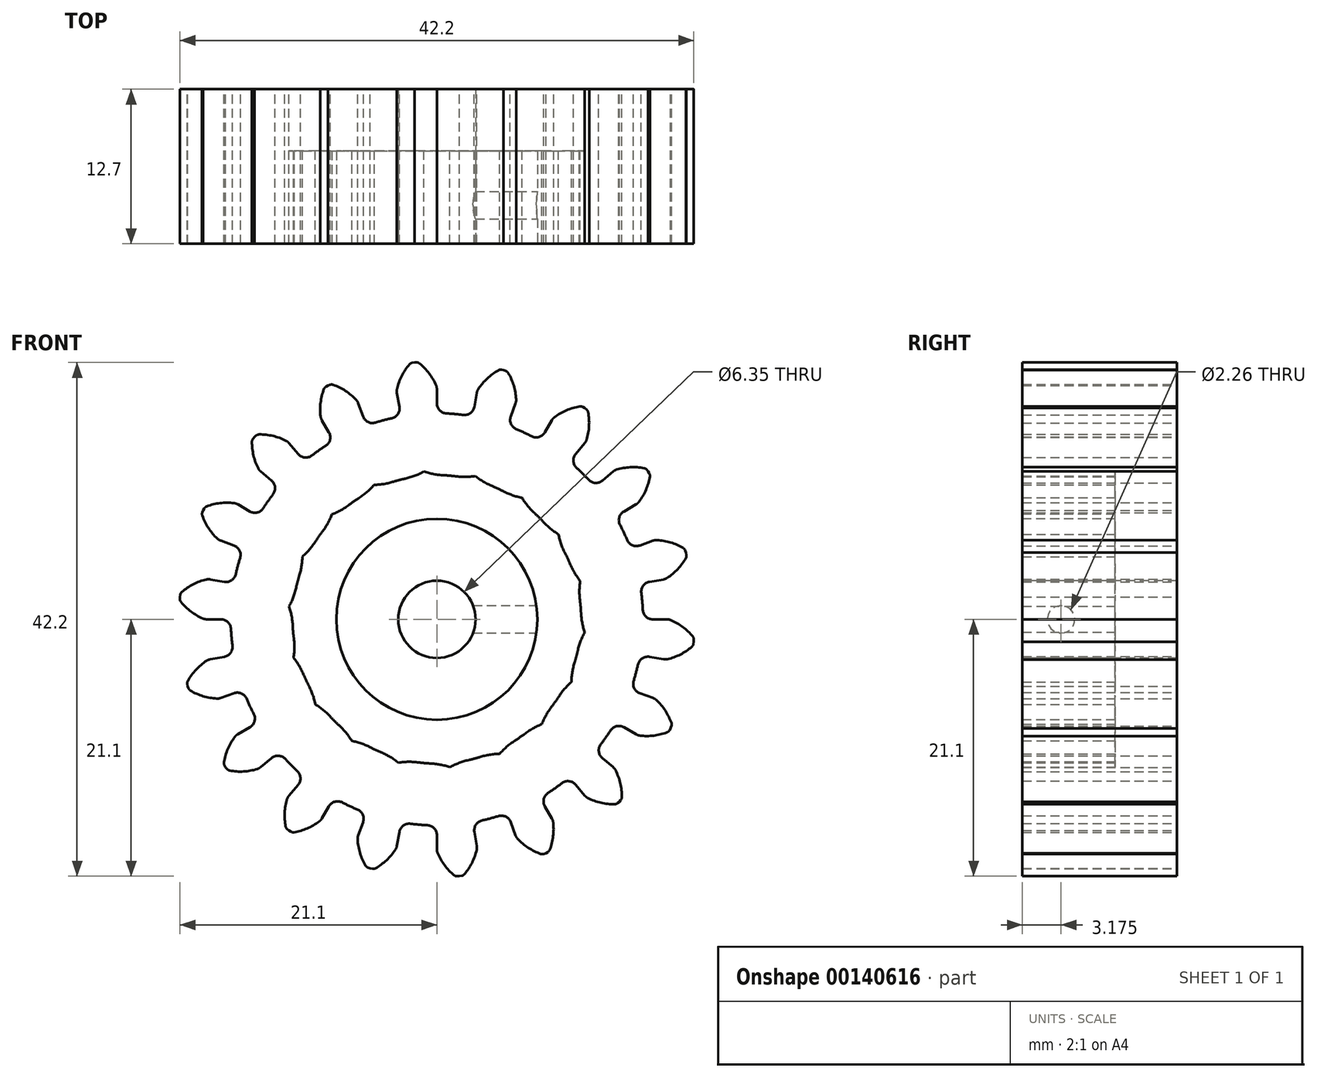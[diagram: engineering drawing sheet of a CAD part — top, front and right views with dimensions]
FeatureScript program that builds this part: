
annotation { "Feature Type Name" : "Feature", "Feature Type Description" : "" }
export const myFeature = defineFeature(function(context is Context, id is Id, definition is map)
    precondition{}
    {
        {
            var Q0;
            Q0=qCreatedBy(makeId("Front.planeOp"),FACE);
            var sketch = newSketch(context, id + "F0", { "sketchPlane" : qUnion([Q0])});
            skArc(sketch, "E0", {"start": v(-3.71, 16.52) * mm, "mid": v(-4.38, 16.35) * mm, "end": v(-5.04, 16.16) * mm});
            skArc(sketch, "E1.trimOffspring", {"start": v(-0.07, 19.21) * mm, "mid": v(-0.63, 20.2) * mm, "end": v(-1.42, 21.02) * mm});
            skLineSegment(sketch, "E2", {"start": v(0, 18.89) * mm, "end": v(0, 17.74) * mm});
            skLineSegment(sketch, "E3", {"start": v(-1.66, 21.1) * mm, "end": v(-1.85, 21.1) * mm});
            skLineSegment(sketch, "E4.MirrorCS", {"start": v(-2.03, 21.07) * mm, "end": v(-1.85, 21.1) * mm});
            skArc(sketch, "E5.MirrorCS", {"start": v(-3.27, 18.93) * mm, "mid": v(-2.88, 20) * mm, "end": v(-2.25, 20.94) * mm});
            skLineSegment(sketch, "E6.MirrorCS", {"start": v(-3.28, 18.6) * mm, "end": v(-3.08, 17.47) * mm});
            skPoint(sketch, "E7.visualSharp", {"position": v(0, 19.05) * mm});
            skArc(sketch, "E7.filletArc", {"start": v(0, 18.89) * mm, "mid": v(-0.02, 19.05) * mm, "end": v(-0.07, 19.21) * mm});
            skPoint(sketch, "E8.visualSharp", {"position": v(-3.3, 18.76) * mm});
            skArc(sketch, "E8.filletArc", {"start": v(-3.27, 18.93) * mm, "mid": v(-3.3, 18.77) * mm, "end": v(-3.28, 18.6) * mm});
            skPoint(sketch, "E9.visualSharp", {"position": v(-2.94, 16.67) * mm});
            skArc(sketch, "E9.filletArc", {"start": v(-3.71, 16.52) * mm, "mid": v(-3.2, 16.86) * mm, "end": v(-3.08, 17.47) * mm});
            skPoint(sketch, "E10.visualSharp", {"position": v(0, 16.93) * mm});
            skArc(sketch, "E10.filletArc", {"start": v(0, 17.74) * mm, "mid": v(0.23, 17.17) * mm, "end": v(0.79, 16.91) * mm});
            skPoint(sketch, "E11.visualSharp", {"position": v(-2.16, 21.05) * mm});
            skArc(sketch, "E11.filletArc", {"start": v(-2.03, 21.07) * mm, "mid": v(-2.15, 21.03) * mm, "end": v(-2.25, 20.94) * mm});
            skPoint(sketch, "E12.visualSharp", {"position": v(-1.53, 21.1) * mm});
            skArc(sketch, "E12.filletArc", {"start": v(-1.42, 21.02) * mm, "mid": v(-1.53, 21.08) * mm, "end": v(-1.66, 21.1) * mm});
            skArc(sketch, "E13.1.0", {"start": v(-9.14, 14.25) * mm, "mid": v(-8.78, 14.75) * mm, "end": v(-8.87, 15.36) * mm});
            skLineSegment(sketch, "E13.1.1", {"start": v(-9.44, 16.36) * mm, "end": v(-8.87, 15.36) * mm});
            skArc(sketch, "E13.1.2", {"start": v(-9.55, 16.67) * mm, "mid": v(-9.51, 16.51) * mm, "end": v(-9.44, 16.36) * mm});
            skArc(sketch, "E13.1.3", {"start": v(-9.55, 16.67) * mm, "mid": v(-9.55, 17.8) * mm, "end": v(-9.28, 18.9) * mm});
            skArc(sketch, "E13.1.4", {"start": v(-9.11, 19.1) * mm, "mid": v(-9.22, 19.02) * mm, "end": v(-9.28, 18.9) * mm});
            skLineSegment(sketch, "E13.1.5", {"start": v(-9.11, 19.1) * mm, "end": v(-8.95, 19.2) * mm});
            skLineSegment(sketch, "E13.1.6", {"start": v(-8.78, 19.26) * mm, "end": v(-8.95, 19.2) * mm});
            skArc(sketch, "E13.1.7", {"start": v(-8.52, 19.26) * mm, "mid": v(-8.65, 19.29) * mm, "end": v(-8.78, 19.26) * mm});
            skArc(sketch, "E13.1.8", {"start": v(-6.63, 18.03) * mm, "mid": v(-7.5, 18.76) * mm, "end": v(-8.52, 19.26) * mm});
            skArc(sketch, "E13.1.9", {"start": v(-6.46, 17.75) * mm, "mid": v(-6.53, 17.9) * mm, "end": v(-6.63, 18.03) * mm});
            skLineSegment(sketch, "E13.1.10", {"start": v(-6.46, 17.75) * mm, "end": v(-6.07, 16.67) * mm});
            skArc(sketch, "E13.1.11", {"start": v(-6.07, 16.67) * mm, "mid": v(-5.66, 16.2) * mm, "end": v(-5.04, 16.16) * mm});
            skArc(sketch, "E13.2.0", {"start": v(-13.46, 10.27) * mm, "mid": v(-13.3, 10.86) * mm, "end": v(-13.59, 11.4) * mm});
            skLineSegment(sketch, "E13.2.1", {"start": v(-14.47, 12.14) * mm, "end": v(-13.59, 11.4) * mm});
            skArc(sketch, "E13.2.2", {"start": v(-14.68, 12.4) * mm, "mid": v(-14.59, 12.26) * mm, "end": v(-14.47, 12.14) * mm});
            skArc(sketch, "E13.2.3", {"start": v(-14.68, 12.4) * mm, "mid": v(-15.06, 13.47) * mm, "end": v(-15.19, 14.6) * mm});
            skArc(sketch, "E13.2.4", {"start": v(-15.1, 14.84) * mm, "mid": v(-15.17, 14.72) * mm, "end": v(-15.19, 14.6) * mm});
            skLineSegment(sketch, "E13.2.5", {"start": v(-15.1, 14.84) * mm, "end": v(-14.98, 14.98) * mm});
            skLineSegment(sketch, "E13.2.6", {"start": v(-14.84, 15.1) * mm, "end": v(-14.98, 14.98) * mm});
            skArc(sketch, "E13.2.7", {"start": v(-14.6, 15.19) * mm, "mid": v(-14.72, 15.17) * mm, "end": v(-14.84, 15.1) * mm});
            skArc(sketch, "E13.2.8", {"start": v(-12.4, 14.68) * mm, "mid": v(-13.47, 15.06) * mm, "end": v(-14.6, 15.19) * mm});
            skArc(sketch, "E13.2.9", {"start": v(-12.14, 14.47) * mm, "mid": v(-12.26, 14.59) * mm, "end": v(-12.4, 14.68) * mm});
            skLineSegment(sketch, "E13.2.10", {"start": v(-12.14, 14.47) * mm, "end": v(-11.4, 13.59) * mm});
            skArc(sketch, "E13.2.11", {"start": v(-11.4, 13.59) * mm, "mid": v(-10.86, 13.3) * mm, "end": v(-10.27, 13.46) * mm});
            skArc(sketch, "E13.3.0", {"start": v(-16.16, 5.04) * mm, "mid": v(-16.2, 5.66) * mm, "end": v(-16.67, 6.07) * mm});
            skLineSegment(sketch, "E13.3.1", {"start": v(-17.75, 6.46) * mm, "end": v(-16.67, 6.07) * mm});
            skArc(sketch, "E13.3.2", {"start": v(-18.03, 6.63) * mm, "mid": v(-17.9, 6.53) * mm, "end": v(-17.75, 6.46) * mm});
            skArc(sketch, "E13.3.3", {"start": v(-18.03, 6.63) * mm, "mid": v(-18.76, 7.5) * mm, "end": v(-19.26, 8.52) * mm});
            skArc(sketch, "E13.3.4", {"start": v(-19.26, 8.78) * mm, "mid": v(-19.29, 8.65) * mm, "end": v(-19.26, 8.52) * mm});
            skLineSegment(sketch, "E13.3.5", {"start": v(-19.26, 8.78) * mm, "end": v(-19.2, 8.95) * mm});
            skLineSegment(sketch, "E13.3.6", {"start": v(-19.1, 9.11) * mm, "end": v(-19.2, 8.95) * mm});
            skArc(sketch, "E13.3.7", {"start": v(-18.9, 9.28) * mm, "mid": v(-19.02, 9.22) * mm, "end": v(-19.1, 9.11) * mm});
            skArc(sketch, "E13.3.8", {"start": v(-16.67, 9.55) * mm, "mid": v(-17.8, 9.55) * mm, "end": v(-18.9, 9.28) * mm});
            skArc(sketch, "E13.3.9", {"start": v(-16.36, 9.44) * mm, "mid": v(-16.51, 9.51) * mm, "end": v(-16.67, 9.55) * mm});
            skLineSegment(sketch, "E13.3.10", {"start": v(-16.36, 9.44) * mm, "end": v(-15.36, 8.87) * mm});
            skArc(sketch, "E13.3.11", {"start": v(-15.36, 8.87) * mm, "mid": v(-14.75, 8.78) * mm, "end": v(-14.25, 9.14) * mm});
            skArc(sketch, "E13.4.0", {"start": v(-16.91, -0.79) * mm, "mid": v(-17.17, -0.23) * mm, "end": v(-17.74, 0) * mm});
            skLineSegment(sketch, "E13.4.1", {"start": v(-18.89, 0) * mm, "end": v(-17.74, 0) * mm});
            skArc(sketch, "E13.4.2", {"start": v(-19.21, 0.07) * mm, "mid": v(-19.05, 0.02) * mm, "end": v(-18.89, 0) * mm});
            skArc(sketch, "E13.4.3", {"start": v(-19.21, 0.07) * mm, "mid": v(-20.2, 0.63) * mm, "end": v(-21.02, 1.42) * mm});
            skArc(sketch, "E13.4.4", {"start": v(-21.1, 1.66) * mm, "mid": v(-21.08, 1.53) * mm, "end": v(-21.02, 1.42) * mm});
            skLineSegment(sketch, "E13.4.5", {"start": v(-21.1, 1.66) * mm, "end": v(-21.1, 1.85) * mm});
            skLineSegment(sketch, "E13.4.6", {"start": v(-21.07, 2.03) * mm, "end": v(-21.1, 1.85) * mm});
            skArc(sketch, "E13.4.7", {"start": v(-20.94, 2.25) * mm, "mid": v(-21.03, 2.15) * mm, "end": v(-21.07, 2.03) * mm});
            skArc(sketch, "E13.4.8", {"start": v(-18.93, 3.27) * mm, "mid": v(-20, 2.88) * mm, "end": v(-20.94, 2.25) * mm});
            skArc(sketch, "E13.4.9", {"start": v(-18.6, 3.28) * mm, "mid": v(-18.77, 3.3) * mm, "end": v(-18.93, 3.27) * mm});
            skLineSegment(sketch, "E13.4.10", {"start": v(-18.6, 3.28) * mm, "end": v(-17.47, 3.08) * mm});
            skArc(sketch, "E13.4.11", {"start": v(-17.47, 3.08) * mm, "mid": v(-16.86, 3.2) * mm, "end": v(-16.52, 3.71) * mm});
            skArc(sketch, "E13.5.0", {"start": v(-15.62, -6.52) * mm, "mid": v(-16.05, -6.09) * mm, "end": v(-16.67, -6.07) * mm});
            skLineSegment(sketch, "E13.5.1", {"start": v(-17.75, -6.46) * mm, "end": v(-16.67, -6.07) * mm});
            skArc(sketch, "E13.5.2", {"start": v(-18.08, -6.5) * mm, "mid": v(-17.91, -6.5) * mm, "end": v(-17.75, -6.46) * mm});
            skArc(sketch, "E13.5.3", {"start": v(-18.08, -6.5) * mm, "mid": v(-19.2, -6.31) * mm, "end": v(-20.23, -5.86) * mm});
            skArc(sketch, "E13.5.4", {"start": v(-20.4, -5.66) * mm, "mid": v(-20.33, -5.77) * mm, "end": v(-20.23, -5.86) * mm});
            skLineSegment(sketch, "E13.5.5", {"start": v(-20.4, -5.66) * mm, "end": v(-20.46, -5.48) * mm});
            skLineSegment(sketch, "E13.5.6", {"start": v(-20.5, -5.3) * mm, "end": v(-20.46, -5.48) * mm});
            skArc(sketch, "E13.5.7", {"start": v(-20.45, -5.04) * mm, "mid": v(-20.5, -5.17) * mm, "end": v(-20.5, -5.3) * mm});
            skArc(sketch, "E13.5.8", {"start": v(-18.91, -3.4) * mm, "mid": v(-19.78, -4.13) * mm, "end": v(-20.45, -5.04) * mm});
            skArc(sketch, "E13.5.9", {"start": v(-18.6, -3.28) * mm, "mid": v(-18.76, -3.33) * mm, "end": v(-18.91, -3.4) * mm});
            skLineSegment(sketch, "E13.5.10", {"start": v(-18.6, -3.28) * mm, "end": v(-17.47, -3.08) * mm});
            skArc(sketch, "E13.5.11", {"start": v(-17.47, -3.08) * mm, "mid": v(-16.94, -2.76) * mm, "end": v(-16.8, -2.16) * mm});
            skArc(sketch, "E13.6.0", {"start": v(-12.45, -11.47) * mm, "mid": v(-13, -11.2) * mm, "end": v(-13.59, -11.4) * mm});
            skLineSegment(sketch, "E13.6.1", {"start": v(-14.47, -12.14) * mm, "end": v(-13.59, -11.4) * mm});
            skArc(sketch, "E13.6.2", {"start": v(-14.76, -12.3) * mm, "mid": v(-14.6, -12.24) * mm, "end": v(-14.47, -12.14) * mm});
            skArc(sketch, "E13.6.3", {"start": v(-14.76, -12.3) * mm, "mid": v(-15.88, -12.5) * mm, "end": v(-17.01, -12.42) * mm});
            skArc(sketch, "E13.6.4", {"start": v(-17.23, -12.3) * mm, "mid": v(-17.13, -12.38) * mm, "end": v(-17.01, -12.42) * mm});
            skLineSegment(sketch, "E13.6.5", {"start": v(-17.23, -12.3) * mm, "end": v(-17.35, -12.15) * mm});
            skLineSegment(sketch, "E13.6.6", {"start": v(-17.45, -11.99) * mm, "end": v(-17.35, -12.15) * mm});
            skArc(sketch, "E13.6.7", {"start": v(-17.5, -11.74) * mm, "mid": v(-17.5, -11.87) * mm, "end": v(-17.45, -11.99) * mm});
            skArc(sketch, "E13.6.8", {"start": v(-16.6, -9.66) * mm, "mid": v(-17.17, -10.65) * mm, "end": v(-17.5, -11.74) * mm});
            skArc(sketch, "E13.6.9", {"start": v(-16.36, -9.44) * mm, "mid": v(-16.5, -9.54) * mm, "end": v(-16.6, -9.66) * mm});
            skLineSegment(sketch, "E13.6.10", {"start": v(-16.36, -9.44) * mm, "end": v(-15.36, -8.87) * mm});
            skArc(sketch, "E13.6.11", {"start": v(-15.36, -8.87) * mm, "mid": v(-14.98, -8.38) * mm, "end": v(-15.04, -7.77) * mm});
            skArc(sketch, "E13.7.0", {"start": v(-7.77, -15.04) * mm, "mid": v(-8.38, -14.98) * mm, "end": v(-8.87, -15.36) * mm});
            skLineSegment(sketch, "E13.7.1", {"start": v(-9.44, -16.36) * mm, "end": v(-8.87, -15.36) * mm});
            skArc(sketch, "E13.7.2", {"start": v(-9.66, -16.6) * mm, "mid": v(-9.54, -16.5) * mm, "end": v(-9.44, -16.36) * mm});
            skArc(sketch, "E13.7.3", {"start": v(-9.66, -16.6) * mm, "mid": v(-10.65, -17.17) * mm, "end": v(-11.74, -17.5) * mm});
            skArc(sketch, "E13.7.4", {"start": v(-11.99, -17.45) * mm, "mid": v(-11.87, -17.5) * mm, "end": v(-11.74, -17.5) * mm});
            skLineSegment(sketch, "E13.7.5", {"start": v(-11.99, -17.45) * mm, "end": v(-12.15, -17.35) * mm});
            skLineSegment(sketch, "E13.7.6", {"start": v(-12.3, -17.23) * mm, "end": v(-12.15, -17.35) * mm});
            skArc(sketch, "E13.7.7", {"start": v(-12.42, -17.01) * mm, "mid": v(-12.38, -17.13) * mm, "end": v(-12.3, -17.23) * mm});
            skArc(sketch, "E13.7.8", {"start": v(-12.3, -14.76) * mm, "mid": v(-12.5, -15.88) * mm, "end": v(-12.42, -17.01) * mm});
            skArc(sketch, "E13.7.9", {"start": v(-12.14, -14.47) * mm, "mid": v(-12.24, -14.6) * mm, "end": v(-12.3, -14.76) * mm});
            skLineSegment(sketch, "E13.7.10", {"start": v(-12.14, -14.47) * mm, "end": v(-11.4, -13.59) * mm});
            skArc(sketch, "E13.7.11", {"start": v(-11.4, -13.59) * mm, "mid": v(-11.2, -13) * mm, "end": v(-11.47, -12.45) * mm});
            skArc(sketch, "E13.8.0", {"start": v(-2.16, -16.8) * mm, "mid": v(-2.76, -16.94) * mm, "end": v(-3.08, -17.47) * mm});
            skLineSegment(sketch, "E13.8.1", {"start": v(-3.28, -18.6) * mm, "end": v(-3.08, -17.47) * mm});
            skArc(sketch, "E13.8.2", {"start": v(-3.4, -18.91) * mm, "mid": v(-3.33, -18.76) * mm, "end": v(-3.28, -18.6) * mm});
            skArc(sketch, "E13.8.3", {"start": v(-3.4, -18.91) * mm, "mid": v(-4.13, -19.78) * mm, "end": v(-5.04, -20.45) * mm});
            skArc(sketch, "E13.8.4", {"start": v(-5.3, -20.5) * mm, "mid": v(-5.17, -20.5) * mm, "end": v(-5.04, -20.45) * mm});
            skLineSegment(sketch, "E13.8.5", {"start": v(-5.3, -20.5) * mm, "end": v(-5.48, -20.46) * mm});
            skLineSegment(sketch, "E13.8.6", {"start": v(-5.66, -20.4) * mm, "end": v(-5.48, -20.46) * mm});
            skArc(sketch, "E13.8.7", {"start": v(-5.86, -20.23) * mm, "mid": v(-5.77, -20.33) * mm, "end": v(-5.66, -20.4) * mm});
            skArc(sketch, "E13.8.8", {"start": v(-6.5, -18.08) * mm, "mid": v(-6.31, -19.2) * mm, "end": v(-5.86, -20.23) * mm});
            skArc(sketch, "E13.8.9", {"start": v(-6.46, -17.75) * mm, "mid": v(-6.5, -17.91) * mm, "end": v(-6.5, -18.08) * mm});
            skLineSegment(sketch, "E13.8.10", {"start": v(-6.46, -17.75) * mm, "end": v(-6.07, -16.67) * mm});
            skArc(sketch, "E13.8.11", {"start": v(-6.07, -16.67) * mm, "mid": v(-6.09, -16.05) * mm, "end": v(-6.52, -15.62) * mm});
            skArc(sketch, "E13.9.0", {"start": v(3.71, -16.52) * mm, "mid": v(3.2, -16.86) * mm, "end": v(3.08, -17.47) * mm});
            skLineSegment(sketch, "E13.9.1", {"start": v(3.28, -18.6) * mm, "end": v(3.08, -17.47) * mm});
            skArc(sketch, "E13.9.2", {"start": v(3.27, -18.93) * mm, "mid": v(3.3, -18.77) * mm, "end": v(3.28, -18.6) * mm});
            skArc(sketch, "E13.9.3", {"start": v(3.27, -18.93) * mm, "mid": v(2.88, -20) * mm, "end": v(2.25, -20.94) * mm});
            skArc(sketch, "E13.9.4", {"start": v(2.03, -21.07) * mm, "mid": v(2.15, -21.03) * mm, "end": v(2.25, -20.94) * mm});
            skLineSegment(sketch, "E13.9.5", {"start": v(2.03, -21.07) * mm, "end": v(1.85, -21.1) * mm});
            skLineSegment(sketch, "E13.9.6", {"start": v(1.66, -21.1) * mm, "end": v(1.85, -21.1) * mm});
            skArc(sketch, "E13.9.7", {"start": v(1.42, -21.02) * mm, "mid": v(1.53, -21.08) * mm, "end": v(1.66, -21.1) * mm});
            skArc(sketch, "E13.9.8", {"start": v(0.07, -19.21) * mm, "mid": v(0.63, -20.2) * mm, "end": v(1.42, -21.02) * mm});
            skArc(sketch, "E13.9.9", {"start": v(0, -18.89) * mm, "mid": v(0.02, -19.05) * mm, "end": v(0.07, -19.21) * mm});
            skLineSegment(sketch, "E13.9.10", {"start": v(0, -18.89) * mm, "end": v(0, -17.74) * mm});
            skArc(sketch, "E13.9.11", {"start": v(0, -17.74) * mm, "mid": v(-0.23, -17.17) * mm, "end": v(-0.79, -16.91) * mm});
            skArc(sketch, "E13.10.0", {"start": v(9.14, -14.25) * mm, "mid": v(8.78, -14.75) * mm, "end": v(8.87, -15.36) * mm});
            skLineSegment(sketch, "E13.10.1", {"start": v(9.44, -16.36) * mm, "end": v(8.87, -15.36) * mm});
            skArc(sketch, "E13.10.2", {"start": v(9.55, -16.67) * mm, "mid": v(9.51, -16.51) * mm, "end": v(9.44, -16.36) * mm});
            skArc(sketch, "E13.10.3", {"start": v(9.55, -16.67) * mm, "mid": v(9.55, -17.8) * mm, "end": v(9.28, -18.9) * mm});
            skArc(sketch, "E13.10.4", {"start": v(9.11, -19.1) * mm, "mid": v(9.22, -19.02) * mm, "end": v(9.28, -18.9) * mm});
            skLineSegment(sketch, "E13.10.5", {"start": v(9.11, -19.1) * mm, "end": v(8.95, -19.2) * mm});
            skLineSegment(sketch, "E13.10.6", {"start": v(8.78, -19.26) * mm, "end": v(8.95, -19.2) * mm});
            skArc(sketch, "E13.10.7", {"start": v(8.52, -19.26) * mm, "mid": v(8.65, -19.29) * mm, "end": v(8.78, -19.26) * mm});
            skArc(sketch, "E13.10.8", {"start": v(6.63, -18.03) * mm, "mid": v(7.5, -18.76) * mm, "end": v(8.52, -19.26) * mm});
            skArc(sketch, "E13.10.9", {"start": v(6.46, -17.75) * mm, "mid": v(6.53, -17.9) * mm, "end": v(6.63, -18.03) * mm});
            skLineSegment(sketch, "E13.10.10", {"start": v(6.46, -17.75) * mm, "end": v(6.07, -16.67) * mm});
            skArc(sketch, "E13.10.11", {"start": v(6.07, -16.67) * mm, "mid": v(5.66, -16.2) * mm, "end": v(5.04, -16.16) * mm});
            skArc(sketch, "E13.11.0", {"start": v(13.46, -10.27) * mm, "mid": v(13.3, -10.86) * mm, "end": v(13.59, -11.4) * mm});
            skLineSegment(sketch, "E13.11.1", {"start": v(14.47, -12.14) * mm, "end": v(13.59, -11.4) * mm});
            skArc(sketch, "E13.11.2", {"start": v(14.68, -12.4) * mm, "mid": v(14.59, -12.26) * mm, "end": v(14.47, -12.14) * mm});
            skArc(sketch, "E13.11.3", {"start": v(14.68, -12.4) * mm, "mid": v(15.06, -13.47) * mm, "end": v(15.19, -14.6) * mm});
            skArc(sketch, "E13.11.4", {"start": v(15.1, -14.84) * mm, "mid": v(15.17, -14.72) * mm, "end": v(15.19, -14.6) * mm});
            skLineSegment(sketch, "E13.11.5", {"start": v(15.1, -14.84) * mm, "end": v(14.98, -14.98) * mm});
            skLineSegment(sketch, "E13.11.6", {"start": v(14.84, -15.1) * mm, "end": v(14.98, -14.98) * mm});
            skArc(sketch, "E13.11.7", {"start": v(14.6, -15.19) * mm, "mid": v(14.72, -15.17) * mm, "end": v(14.84, -15.1) * mm});
            skArc(sketch, "E13.11.8", {"start": v(12.4, -14.68) * mm, "mid": v(13.47, -15.06) * mm, "end": v(14.6, -15.19) * mm});
            skArc(sketch, "E13.11.9", {"start": v(12.14, -14.47) * mm, "mid": v(12.26, -14.59) * mm, "end": v(12.4, -14.68) * mm});
            skLineSegment(sketch, "E13.11.10", {"start": v(12.14, -14.47) * mm, "end": v(11.4, -13.59) * mm});
            skArc(sketch, "E13.11.11", {"start": v(11.4, -13.59) * mm, "mid": v(10.86, -13.3) * mm, "end": v(10.27, -13.46) * mm});
            skArc(sketch, "E13.12.0", {"start": v(16.16, -5.04) * mm, "mid": v(16.2, -5.66) * mm, "end": v(16.67, -6.07) * mm});
            skLineSegment(sketch, "E13.12.1", {"start": v(17.75, -6.46) * mm, "end": v(16.67, -6.07) * mm});
            skArc(sketch, "E13.12.2", {"start": v(18.03, -6.63) * mm, "mid": v(17.9, -6.53) * mm, "end": v(17.75, -6.46) * mm});
            skArc(sketch, "E13.12.3", {"start": v(18.03, -6.63) * mm, "mid": v(18.76, -7.5) * mm, "end": v(19.26, -8.52) * mm});
            skArc(sketch, "E13.12.4", {"start": v(19.26, -8.78) * mm, "mid": v(19.29, -8.65) * mm, "end": v(19.26, -8.52) * mm});
            skLineSegment(sketch, "E13.12.5", {"start": v(19.26, -8.78) * mm, "end": v(19.2, -8.95) * mm});
            skLineSegment(sketch, "E13.12.6", {"start": v(19.1, -9.11) * mm, "end": v(19.2, -8.95) * mm});
            skArc(sketch, "E13.12.7", {"start": v(18.9, -9.28) * mm, "mid": v(19.02, -9.22) * mm, "end": v(19.1, -9.11) * mm});
            skArc(sketch, "E13.12.8", {"start": v(16.67, -9.55) * mm, "mid": v(17.8, -9.55) * mm, "end": v(18.9, -9.28) * mm});
            skArc(sketch, "E13.12.9", {"start": v(16.36, -9.44) * mm, "mid": v(16.51, -9.51) * mm, "end": v(16.67, -9.55) * mm});
            skLineSegment(sketch, "E13.12.10", {"start": v(16.36, -9.44) * mm, "end": v(15.36, -8.87) * mm});
            skArc(sketch, "E13.12.11", {"start": v(15.36, -8.87) * mm, "mid": v(14.75, -8.78) * mm, "end": v(14.25, -9.14) * mm});
            skArc(sketch, "E13.13.0", {"start": v(16.91, 0.79) * mm, "mid": v(17.17, 0.23) * mm, "end": v(17.74, 0) * mm});
            skLineSegment(sketch, "E13.13.1", {"start": v(18.89, 0) * mm, "end": v(17.74, 0) * mm});
            skArc(sketch, "E13.13.2", {"start": v(19.21, -0.07) * mm, "mid": v(19.05, -0.02) * mm, "end": v(18.89, 0) * mm});
            skArc(sketch, "E13.13.3", {"start": v(19.21, -0.07) * mm, "mid": v(20.2, -0.63) * mm, "end": v(21.02, -1.42) * mm});
            skArc(sketch, "E13.13.4", {"start": v(21.1, -1.66) * mm, "mid": v(21.08, -1.53) * mm, "end": v(21.02, -1.42) * mm});
            skLineSegment(sketch, "E13.13.5", {"start": v(21.1, -1.66) * mm, "end": v(21.1, -1.85) * mm});
            skLineSegment(sketch, "E13.13.6", {"start": v(21.07, -2.03) * mm, "end": v(21.1, -1.85) * mm});
            skArc(sketch, "E13.13.7", {"start": v(20.94, -2.25) * mm, "mid": v(21.03, -2.15) * mm, "end": v(21.07, -2.03) * mm});
            skArc(sketch, "E13.13.8", {"start": v(18.93, -3.27) * mm, "mid": v(20, -2.88) * mm, "end": v(20.94, -2.25) * mm});
            skArc(sketch, "E13.13.9", {"start": v(18.6, -3.28) * mm, "mid": v(18.77, -3.3) * mm, "end": v(18.93, -3.27) * mm});
            skLineSegment(sketch, "E13.13.10", {"start": v(18.6, -3.28) * mm, "end": v(17.47, -3.08) * mm});
            skArc(sketch, "E13.13.11", {"start": v(17.47, -3.08) * mm, "mid": v(16.86, -3.2) * mm, "end": v(16.52, -3.71) * mm});
            skArc(sketch, "E13.14.0", {"start": v(15.62, 6.52) * mm, "mid": v(16.05, 6.09) * mm, "end": v(16.67, 6.07) * mm});
            skLineSegment(sketch, "E13.14.1", {"start": v(17.75, 6.46) * mm, "end": v(16.67, 6.07) * mm});
            skArc(sketch, "E13.14.2", {"start": v(18.08, 6.5) * mm, "mid": v(17.91, 6.5) * mm, "end": v(17.75, 6.46) * mm});
            skArc(sketch, "E13.14.3", {"start": v(18.08, 6.5) * mm, "mid": v(19.2, 6.31) * mm, "end": v(20.23, 5.86) * mm});
            skArc(sketch, "E13.14.4", {"start": v(20.4, 5.66) * mm, "mid": v(20.33, 5.77) * mm, "end": v(20.23, 5.86) * mm});
            skLineSegment(sketch, "E13.14.5", {"start": v(20.4, 5.66) * mm, "end": v(20.46, 5.48) * mm});
            skLineSegment(sketch, "E13.14.6", {"start": v(20.5, 5.3) * mm, "end": v(20.46, 5.48) * mm});
            skArc(sketch, "E13.14.7", {"start": v(20.45, 5.04) * mm, "mid": v(20.5, 5.17) * mm, "end": v(20.5, 5.3) * mm});
            skArc(sketch, "E13.14.8", {"start": v(18.91, 3.4) * mm, "mid": v(19.78, 4.13) * mm, "end": v(20.45, 5.04) * mm});
            skArc(sketch, "E13.14.9", {"start": v(18.6, 3.28) * mm, "mid": v(18.76, 3.33) * mm, "end": v(18.91, 3.4) * mm});
            skLineSegment(sketch, "E13.14.10", {"start": v(18.6, 3.28) * mm, "end": v(17.47, 3.08) * mm});
            skArc(sketch, "E13.14.11", {"start": v(17.47, 3.08) * mm, "mid": v(16.94, 2.76) * mm, "end": v(16.8, 2.16) * mm});
            skArc(sketch, "E13.15.0", {"start": v(12.45, 11.47) * mm, "mid": v(13, 11.2) * mm, "end": v(13.59, 11.4) * mm});
            skLineSegment(sketch, "E13.15.1", {"start": v(14.47, 12.14) * mm, "end": v(13.59, 11.4) * mm});
            skArc(sketch, "E13.15.2", {"start": v(14.76, 12.3) * mm, "mid": v(14.6, 12.24) * mm, "end": v(14.47, 12.14) * mm});
            skArc(sketch, "E13.15.3", {"start": v(14.76, 12.3) * mm, "mid": v(15.88, 12.5) * mm, "end": v(17.01, 12.42) * mm});
            skArc(sketch, "E13.15.4", {"start": v(17.23, 12.3) * mm, "mid": v(17.13, 12.38) * mm, "end": v(17.01, 12.42) * mm});
            skLineSegment(sketch, "E13.15.5", {"start": v(17.23, 12.3) * mm, "end": v(17.35, 12.15) * mm});
            skLineSegment(sketch, "E13.15.6", {"start": v(17.45, 11.99) * mm, "end": v(17.35, 12.15) * mm});
            skArc(sketch, "E13.15.7", {"start": v(17.5, 11.74) * mm, "mid": v(17.5, 11.87) * mm, "end": v(17.45, 11.99) * mm});
            skArc(sketch, "E13.15.8", {"start": v(16.6, 9.66) * mm, "mid": v(17.17, 10.65) * mm, "end": v(17.5, 11.74) * mm});
            skArc(sketch, "E13.15.9", {"start": v(16.36, 9.44) * mm, "mid": v(16.5, 9.54) * mm, "end": v(16.6, 9.66) * mm});
            skLineSegment(sketch, "E13.15.10", {"start": v(16.36, 9.44) * mm, "end": v(15.36, 8.87) * mm});
            skArc(sketch, "E13.15.11", {"start": v(15.36, 8.87) * mm, "mid": v(14.98, 8.38) * mm, "end": v(15.04, 7.77) * mm});
            skArc(sketch, "E13.16.0", {"start": v(7.77, 15.04) * mm, "mid": v(8.38, 14.98) * mm, "end": v(8.87, 15.36) * mm});
            skLineSegment(sketch, "E13.16.1", {"start": v(9.44, 16.36) * mm, "end": v(8.87, 15.36) * mm});
            skArc(sketch, "E13.16.2", {"start": v(9.66, 16.6) * mm, "mid": v(9.54, 16.5) * mm, "end": v(9.44, 16.36) * mm});
            skArc(sketch, "E13.16.3", {"start": v(9.66, 16.6) * mm, "mid": v(10.65, 17.17) * mm, "end": v(11.74, 17.5) * mm});
            skArc(sketch, "E13.16.4", {"start": v(11.99, 17.45) * mm, "mid": v(11.87, 17.5) * mm, "end": v(11.74, 17.5) * mm});
            skLineSegment(sketch, "E13.16.5", {"start": v(11.99, 17.45) * mm, "end": v(12.15, 17.35) * mm});
            skLineSegment(sketch, "E13.16.6", {"start": v(12.3, 17.23) * mm, "end": v(12.15, 17.35) * mm});
            skArc(sketch, "E13.16.7", {"start": v(12.42, 17.01) * mm, "mid": v(12.38, 17.13) * mm, "end": v(12.3, 17.23) * mm});
            skArc(sketch, "E13.16.8", {"start": v(12.3, 14.76) * mm, "mid": v(12.5, 15.88) * mm, "end": v(12.42, 17.01) * mm});
            skArc(sketch, "E13.16.9", {"start": v(12.14, 14.47) * mm, "mid": v(12.24, 14.6) * mm, "end": v(12.3, 14.76) * mm});
            skLineSegment(sketch, "E13.16.10", {"start": v(12.14, 14.47) * mm, "end": v(11.4, 13.59) * mm});
            skArc(sketch, "E13.16.11", {"start": v(11.4, 13.59) * mm, "mid": v(11.2, 13) * mm, "end": v(11.47, 12.45) * mm});
            skArc(sketch, "E13.17.0", {"start": v(2.16, 16.8) * mm, "mid": v(2.76, 16.94) * mm, "end": v(3.08, 17.47) * mm});
            skLineSegment(sketch, "E13.17.1", {"start": v(3.28, 18.6) * mm, "end": v(3.08, 17.47) * mm});
            skArc(sketch, "E13.17.2", {"start": v(3.4, 18.91) * mm, "mid": v(3.33, 18.76) * mm, "end": v(3.28, 18.6) * mm});
            skArc(sketch, "E13.17.3", {"start": v(3.4, 18.91) * mm, "mid": v(4.13, 19.78) * mm, "end": v(5.04, 20.45) * mm});
            skArc(sketch, "E13.17.4", {"start": v(5.3, 20.5) * mm, "mid": v(5.17, 20.5) * mm, "end": v(5.04, 20.45) * mm});
            skLineSegment(sketch, "E13.17.5", {"start": v(5.3, 20.5) * mm, "end": v(5.48, 20.46) * mm});
            skLineSegment(sketch, "E13.17.6", {"start": v(5.66, 20.4) * mm, "end": v(5.48, 20.46) * mm});
            skArc(sketch, "E13.17.7", {"start": v(5.86, 20.23) * mm, "mid": v(5.77, 20.33) * mm, "end": v(5.66, 20.4) * mm});
            skArc(sketch, "E13.17.8", {"start": v(6.5, 18.08) * mm, "mid": v(6.31, 19.2) * mm, "end": v(5.86, 20.23) * mm});
            skArc(sketch, "E13.17.9", {"start": v(6.46, 17.75) * mm, "mid": v(6.5, 17.91) * mm, "end": v(6.5, 18.08) * mm});
            skLineSegment(sketch, "E13.17.10", {"start": v(6.46, 17.75) * mm, "end": v(6.07, 16.67) * mm});
            skArc(sketch, "E13.17.11", {"start": v(6.07, 16.67) * mm, "mid": v(6.09, 16.05) * mm, "end": v(6.52, 15.62) * mm});
            skArc(sketch, "E14.trimOffspring", {"start": v(-9.14, 14.25) * mm, "mid": v(-9.71, 13.87) * mm, "end": v(-10.27, 13.46) * mm});
            skArc(sketch, "E15.trimOffspring", {"start": v(2.16, 16.8) * mm, "mid": v(1.48, 16.86) * mm, "end": v(0.79, 16.91) * mm});
            skArc(sketch, "E16.trimOffspring", {"start": v(7.77, 15.04) * mm, "mid": v(7.15, 15.34) * mm, "end": v(6.52, 15.62) * mm});
            skArc(sketch, "E17.trimOffspring", {"start": v(12.45, 11.47) * mm, "mid": v(11.97, 11.97) * mm, "end": v(11.47, 12.45) * mm});
            skArc(sketch, "E18.trimOffspring", {"start": v(15.62, 6.52) * mm, "mid": v(15.34, 7.15) * mm, "end": v(15.04, 7.77) * mm});
            skArc(sketch, "E19.trimOffspring", {"start": v(16.91, 0.79) * mm, "mid": v(16.86, 1.48) * mm, "end": v(16.8, 2.16) * mm});
            skArc(sketch, "E20.trimOffspring", {"start": v(16.16, -5.04) * mm, "mid": v(16.35, -4.38) * mm, "end": v(16.52, -3.71) * mm});
            skArc(sketch, "E21.trimOffspring", {"start": v(13.46, -10.27) * mm, "mid": v(13.87, -9.71) * mm, "end": v(14.25, -9.14) * mm});
            skArc(sketch, "E22.trimOffspring", {"start": v(9.14, -14.25) * mm, "mid": v(9.71, -13.87) * mm, "end": v(10.27, -13.46) * mm});
            skArc(sketch, "E23.trimOffspring", {"start": v(3.71, -16.52) * mm, "mid": v(4.38, -16.35) * mm, "end": v(5.04, -16.16) * mm});
            skArc(sketch, "E24.trimOffspring", {"start": v(-2.16, -16.8) * mm, "mid": v(-1.48, -16.86) * mm, "end": v(-0.79, -16.91) * mm});
            skArc(sketch, "E25.trimOffspring", {"start": v(-7.77, -15.04) * mm, "mid": v(-7.15, -15.34) * mm, "end": v(-6.52, -15.62) * mm});
            skArc(sketch, "E26.trimOffspring", {"start": v(-12.45, -11.47) * mm, "mid": v(-11.97, -11.97) * mm, "end": v(-11.47, -12.45) * mm});
            skArc(sketch, "E27.trimOffspring", {"start": v(-15.62, -6.52) * mm, "mid": v(-15.34, -7.15) * mm, "end": v(-15.04, -7.77) * mm});
            skArc(sketch, "E28.trimOffspring", {"start": v(-16.91, -0.79) * mm, "mid": v(-16.86, -1.48) * mm, "end": v(-16.8, -2.16) * mm});
            skArc(sketch, "E29.trimOffspring", {"start": v(-16.16, 5.04) * mm, "mid": v(-16.35, 4.38) * mm, "end": v(-16.52, 3.71) * mm});
            skArc(sketch, "E30.trimOffspring", {"start": v(-13.46, 10.27) * mm, "mid": v(-13.87, 9.71) * mm, "end": v(-14.25, 9.14) * mm});
            skSolve(sketch);
        }
        {
            var Q0;
            Q0 = qSketchRegion(id + "F0", true);
            extrude(context, id + "F1", {"entities" : qUnion([Q0]), "depth" : 12.7 * mm});
        }
        {
            var Q0;
            Q0=makeQuery(id+"F1.opExtrude","CAP_FACE",FACE,{"disambiguationData":[OSD([sQuery(id+"F0.wireOp",EDGE,"E0"),sQuery(id+"F0.wireOp",EDGE,"E1.trimOffspring"),sQuery(id+"F0.wireOp",EDGE,"E2"),sQuery(id+"F0.wireOp",EDGE,"E3"),sQuery(id+"F0.wireOp",EDGE,"E4.MirrorCS"),sQuery(id+"F0.wireOp",EDGE,"E5.MirrorCS"),sQuery(id+"F0.wireOp",EDGE,"E6.MirrorCS"),sQuery(id+"F0.wireOp",EDGE,"E7.filletArc"),sQuery(id+"F0.wireOp",EDGE,"E8.filletArc"),sQuery(id+"F0.wireOp",EDGE,"E9.filletArc"),sQuery(id+"F0.wireOp",EDGE,"E10.filletArc"),sQuery(id+"F0.wireOp",EDGE,"E11.filletArc"),sQuery(id+"F0.wireOp",EDGE,"E12.filletArc"),sQuery(id+"F0.wireOp",EDGE,"E13.1.0"),sQuery(id+"F0.wireOp",EDGE,"E13.1.1"),sQuery(id+"F0.wireOp",EDGE,"E13.1.2"),sQuery(id+"F0.wireOp",EDGE,"E13.1.3"),sQuery(id+"F0.wireOp",EDGE,"E13.1.4"),sQuery(id+"F0.wireOp",EDGE,"E13.1.5"),sQuery(id+"F0.wireOp",EDGE,"E13.1.6"),sQuery(id+"F0.wireOp",EDGE,"E13.1.7"),sQuery(id+"F0.wireOp",EDGE,"E13.1.8"),sQuery(id+"F0.wireOp",EDGE,"E13.1.9"),sQuery(id+"F0.wireOp",EDGE,"E13.1.10"),sQuery(id+"F0.wireOp",EDGE,"E13.1.11"),sQuery(id+"F0.wireOp",EDGE,"E13.2.0"),sQuery(id+"F0.wireOp",EDGE,"E13.2.1"),sQuery(id+"F0.wireOp",EDGE,"E13.2.2"),sQuery(id+"F0.wireOp",EDGE,"E13.2.3"),sQuery(id+"F0.wireOp",EDGE,"E13.2.4"),sQuery(id+"F0.wireOp",EDGE,"E13.2.5"),sQuery(id+"F0.wireOp",EDGE,"E13.2.6"),sQuery(id+"F0.wireOp",EDGE,"E13.2.7"),sQuery(id+"F0.wireOp",EDGE,"E13.2.8"),sQuery(id+"F0.wireOp",EDGE,"E13.2.9"),sQuery(id+"F0.wireOp",EDGE,"E13.2.10"),sQuery(id+"F0.wireOp",EDGE,"E13.2.11"),sQuery(id+"F0.wireOp",EDGE,"E13.3.0"),sQuery(id+"F0.wireOp",EDGE,"E13.3.1"),sQuery(id+"F0.wireOp",EDGE,"E13.3.2"),sQuery(id+"F0.wireOp",EDGE,"E13.3.3"),sQuery(id+"F0.wireOp",EDGE,"E13.3.4"),sQuery(id+"F0.wireOp",EDGE,"E13.3.5"),sQuery(id+"F0.wireOp",EDGE,"E13.3.6"),sQuery(id+"F0.wireOp",EDGE,"E13.3.7"),sQuery(id+"F0.wireOp",EDGE,"E13.3.8"),sQuery(id+"F0.wireOp",EDGE,"E13.3.9"),sQuery(id+"F0.wireOp",EDGE,"E13.3.10"),sQuery(id+"F0.wireOp",EDGE,"E13.3.11"),sQuery(id+"F0.wireOp",EDGE,"E13.4.0"),sQuery(id+"F0.wireOp",EDGE,"E13.4.1"),sQuery(id+"F0.wireOp",EDGE,"E13.4.2"),sQuery(id+"F0.wireOp",EDGE,"E13.4.3"),sQuery(id+"F0.wireOp",EDGE,"E13.4.4"),sQuery(id+"F0.wireOp",EDGE,"E13.4.5"),sQuery(id+"F0.wireOp",EDGE,"E13.4.6"),sQuery(id+"F0.wireOp",EDGE,"E13.4.7"),sQuery(id+"F0.wireOp",EDGE,"E13.4.8"),sQuery(id+"F0.wireOp",EDGE,"E13.4.9"),sQuery(id+"F0.wireOp",EDGE,"E13.4.10"),sQuery(id+"F0.wireOp",EDGE,"E13.4.11"),sQuery(id+"F0.wireOp",EDGE,"E13.5.0"),sQuery(id+"F0.wireOp",EDGE,"E13.5.1"),sQuery(id+"F0.wireOp",EDGE,"E13.5.2"),sQuery(id+"F0.wireOp",EDGE,"E13.5.3"),sQuery(id+"F0.wireOp",EDGE,"E13.5.4"),sQuery(id+"F0.wireOp",EDGE,"E13.5.5"),sQuery(id+"F0.wireOp",EDGE,"E13.5.6"),sQuery(id+"F0.wireOp",EDGE,"E13.5.7"),sQuery(id+"F0.wireOp",EDGE,"E13.5.8"),sQuery(id+"F0.wireOp",EDGE,"E13.5.9"),sQuery(id+"F0.wireOp",EDGE,"E13.5.10"),sQuery(id+"F0.wireOp",EDGE,"E13.5.11"),sQuery(id+"F0.wireOp",EDGE,"E13.6.0"),sQuery(id+"F0.wireOp",EDGE,"E13.6.1"),sQuery(id+"F0.wireOp",EDGE,"E13.6.2"),sQuery(id+"F0.wireOp",EDGE,"E13.6.3"),sQuery(id+"F0.wireOp",EDGE,"E13.6.4"),sQuery(id+"F0.wireOp",EDGE,"E13.6.5"),sQuery(id+"F0.wireOp",EDGE,"E13.6.6"),sQuery(id+"F0.wireOp",EDGE,"E13.6.7"),sQuery(id+"F0.wireOp",EDGE,"E13.6.8"),sQuery(id+"F0.wireOp",EDGE,"E13.6.9"),sQuery(id+"F0.wireOp",EDGE,"E13.6.10"),sQuery(id+"F0.wireOp",EDGE,"E13.6.11"),sQuery(id+"F0.wireOp",EDGE,"E13.7.0"),sQuery(id+"F0.wireOp",EDGE,"E13.7.1"),sQuery(id+"F0.wireOp",EDGE,"E13.7.2"),sQuery(id+"F0.wireOp",EDGE,"E13.7.3"),sQuery(id+"F0.wireOp",EDGE,"E13.7.4"),sQuery(id+"F0.wireOp",EDGE,"E13.7.5"),sQuery(id+"F0.wireOp",EDGE,"E13.7.6"),sQuery(id+"F0.wireOp",EDGE,"E13.7.7"),sQuery(id+"F0.wireOp",EDGE,"E13.7.8"),sQuery(id+"F0.wireOp",EDGE,"E13.7.9"),sQuery(id+"F0.wireOp",EDGE,"E13.7.10"),sQuery(id+"F0.wireOp",EDGE,"E13.7.11"),sQuery(id+"F0.wireOp",EDGE,"E13.8.0"),sQuery(id+"F0.wireOp",EDGE,"E13.8.1"),sQuery(id+"F0.wireOp",EDGE,"E13.8.2"),sQuery(id+"F0.wireOp",EDGE,"E13.8.3"),sQuery(id+"F0.wireOp",EDGE,"E13.8.4"),sQuery(id+"F0.wireOp",EDGE,"E13.8.5"),sQuery(id+"F0.wireOp",EDGE,"E13.8.6"),sQuery(id+"F0.wireOp",EDGE,"E13.8.7"),sQuery(id+"F0.wireOp",EDGE,"E13.8.8"),sQuery(id+"F0.wireOp",EDGE,"E13.8.9"),sQuery(id+"F0.wireOp",EDGE,"E13.8.10"),sQuery(id+"F0.wireOp",EDGE,"E13.8.11"),sQuery(id+"F0.wireOp",EDGE,"E13.9.0"),sQuery(id+"F0.wireOp",EDGE,"E13.9.1"),sQuery(id+"F0.wireOp",EDGE,"E13.9.2"),sQuery(id+"F0.wireOp",EDGE,"E13.9.3"),sQuery(id+"F0.wireOp",EDGE,"E13.9.4"),sQuery(id+"F0.wireOp",EDGE,"E13.9.5"),sQuery(id+"F0.wireOp",EDGE,"E13.9.6"),sQuery(id+"F0.wireOp",EDGE,"E13.9.7"),sQuery(id+"F0.wireOp",EDGE,"E13.9.8"),sQuery(id+"F0.wireOp",EDGE,"E13.9.9"),sQuery(id+"F0.wireOp",EDGE,"E13.9.10"),sQuery(id+"F0.wireOp",EDGE,"E13.9.11"),sQuery(id+"F0.wireOp",EDGE,"E13.10.0"),sQuery(id+"F0.wireOp",EDGE,"E13.10.1"),sQuery(id+"F0.wireOp",EDGE,"E13.10.2"),sQuery(id+"F0.wireOp",EDGE,"E13.10.3"),sQuery(id+"F0.wireOp",EDGE,"E13.10.4"),sQuery(id+"F0.wireOp",EDGE,"E13.10.5"),sQuery(id+"F0.wireOp",EDGE,"E13.10.6"),sQuery(id+"F0.wireOp",EDGE,"E13.10.7"),sQuery(id+"F0.wireOp",EDGE,"E13.10.8"),sQuery(id+"F0.wireOp",EDGE,"E13.10.9"),sQuery(id+"F0.wireOp",EDGE,"E13.10.10"),sQuery(id+"F0.wireOp",EDGE,"E13.10.11"),sQuery(id+"F0.wireOp",EDGE,"E13.11.0"),sQuery(id+"F0.wireOp",EDGE,"E13.11.1"),sQuery(id+"F0.wireOp",EDGE,"E13.11.2"),sQuery(id+"F0.wireOp",EDGE,"E13.11.3"),sQuery(id+"F0.wireOp",EDGE,"E13.11.4"),sQuery(id+"F0.wireOp",EDGE,"E13.11.5"),sQuery(id+"F0.wireOp",EDGE,"E13.11.6"),sQuery(id+"F0.wireOp",EDGE,"E13.11.7"),sQuery(id+"F0.wireOp",EDGE,"E13.11.8"),sQuery(id+"F0.wireOp",EDGE,"E13.11.9"),sQuery(id+"F0.wireOp",EDGE,"E13.11.10"),sQuery(id+"F0.wireOp",EDGE,"E13.11.11"),sQuery(id+"F0.wireOp",EDGE,"E13.12.0"),sQuery(id+"F0.wireOp",EDGE,"E13.12.1"),sQuery(id+"F0.wireOp",EDGE,"E13.12.2"),sQuery(id+"F0.wireOp",EDGE,"E13.12.3"),sQuery(id+"F0.wireOp",EDGE,"E13.12.4"),sQuery(id+"F0.wireOp",EDGE,"E13.12.5"),sQuery(id+"F0.wireOp",EDGE,"E13.12.6"),sQuery(id+"F0.wireOp",EDGE,"E13.12.7"),sQuery(id+"F0.wireOp",EDGE,"E13.12.8"),sQuery(id+"F0.wireOp",EDGE,"E13.12.9"),sQuery(id+"F0.wireOp",EDGE,"E13.12.10"),sQuery(id+"F0.wireOp",EDGE,"E13.12.11"),sQuery(id+"F0.wireOp",EDGE,"E13.13.0"),sQuery(id+"F0.wireOp",EDGE,"E13.13.1"),sQuery(id+"F0.wireOp",EDGE,"E13.13.2"),sQuery(id+"F0.wireOp",EDGE,"E13.13.3"),sQuery(id+"F0.wireOp",EDGE,"E13.13.4"),sQuery(id+"F0.wireOp",EDGE,"E13.13.5"),sQuery(id+"F0.wireOp",EDGE,"E13.13.6"),sQuery(id+"F0.wireOp",EDGE,"E13.13.7"),sQuery(id+"F0.wireOp",EDGE,"E13.13.8"),sQuery(id+"F0.wireOp",EDGE,"E13.13.9"),sQuery(id+"F0.wireOp",EDGE,"E13.13.10"),sQuery(id+"F0.wireOp",EDGE,"E13.13.11"),sQuery(id+"F0.wireOp",EDGE,"E13.14.0"),sQuery(id+"F0.wireOp",EDGE,"E13.14.1"),sQuery(id+"F0.wireOp",EDGE,"E13.14.2"),sQuery(id+"F0.wireOp",EDGE,"E13.14.3"),sQuery(id+"F0.wireOp",EDGE,"E13.14.4"),sQuery(id+"F0.wireOp",EDGE,"E13.14.5"),sQuery(id+"F0.wireOp",EDGE,"E13.14.6"),sQuery(id+"F0.wireOp",EDGE,"E13.14.7"),sQuery(id+"F0.wireOp",EDGE,"E13.14.8"),sQuery(id+"F0.wireOp",EDGE,"E13.14.9"),sQuery(id+"F0.wireOp",EDGE,"E13.14.10"),sQuery(id+"F0.wireOp",EDGE,"E13.14.11"),sQuery(id+"F0.wireOp",EDGE,"E13.15.0"),sQuery(id+"F0.wireOp",EDGE,"E13.15.1"),sQuery(id+"F0.wireOp",EDGE,"E13.15.2"),sQuery(id+"F0.wireOp",EDGE,"E13.15.3"),sQuery(id+"F0.wireOp",EDGE,"E13.15.4"),sQuery(id+"F0.wireOp",EDGE,"E13.15.5"),sQuery(id+"F0.wireOp",EDGE,"E13.15.6"),sQuery(id+"F0.wireOp",EDGE,"E13.15.7"),sQuery(id+"F0.wireOp",EDGE,"E13.15.8"),sQuery(id+"F0.wireOp",EDGE,"E13.15.9"),sQuery(id+"F0.wireOp",EDGE,"E13.15.10"),sQuery(id+"F0.wireOp",EDGE,"E13.15.11"),sQuery(id+"F0.wireOp",EDGE,"E13.16.0"),sQuery(id+"F0.wireOp",EDGE,"E13.16.1"),sQuery(id+"F0.wireOp",EDGE,"E13.16.2"),sQuery(id+"F0.wireOp",EDGE,"E13.16.3"),sQuery(id+"F0.wireOp",EDGE,"E13.16.4"),sQuery(id+"F0.wireOp",EDGE,"E13.16.5"),sQuery(id+"F0.wireOp",EDGE,"E13.16.6"),sQuery(id+"F0.wireOp",EDGE,"E13.16.7"),sQuery(id+"F0.wireOp",EDGE,"E13.16.8"),sQuery(id+"F0.wireOp",EDGE,"E13.16.9"),sQuery(id+"F0.wireOp",EDGE,"E13.16.10"),sQuery(id+"F0.wireOp",EDGE,"E13.16.11"),sQuery(id+"F0.wireOp",EDGE,"E13.17.0"),sQuery(id+"F0.wireOp",EDGE,"E13.17.1"),sQuery(id+"F0.wireOp",EDGE,"E13.17.2"),sQuery(id+"F0.wireOp",EDGE,"E13.17.3"),sQuery(id+"F0.wireOp",EDGE,"E13.17.4"),sQuery(id+"F0.wireOp",EDGE,"E13.17.5"),sQuery(id+"F0.wireOp",EDGE,"E13.17.6"),sQuery(id+"F0.wireOp",EDGE,"E13.17.7"),sQuery(id+"F0.wireOp",EDGE,"E13.17.8"),sQuery(id+"F0.wireOp",EDGE,"E13.17.9"),sQuery(id+"F0.wireOp",EDGE,"E13.17.10"),sQuery(id+"F0.wireOp",EDGE,"E13.17.11"),sQuery(id+"F0.wireOp",EDGE,"E14.trimOffspring"),sQuery(id+"F0.wireOp",EDGE,"E15.trimOffspring"),sQuery(id+"F0.wireOp",EDGE,"E16.trimOffspring"),sQuery(id+"F0.wireOp",EDGE,"E17.trimOffspring"),sQuery(id+"F0.wireOp",EDGE,"E18.trimOffspring"),sQuery(id+"F0.wireOp",EDGE,"E19.trimOffspring"),sQuery(id+"F0.wireOp",EDGE,"E20.trimOffspring"),sQuery(id+"F0.wireOp",EDGE,"E21.trimOffspring"),sQuery(id+"F0.wireOp",EDGE,"E22.trimOffspring"),sQuery(id+"F0.wireOp",EDGE,"E23.trimOffspring"),sQuery(id+"F0.wireOp",EDGE,"E24.trimOffspring"),sQuery(id+"F0.wireOp",EDGE,"E25.trimOffspring"),sQuery(id+"F0.wireOp",EDGE,"E26.trimOffspring"),sQuery(id+"F0.wireOp",EDGE,"E27.trimOffspring"),sQuery(id+"F0.wireOp",EDGE,"E28.trimOffspring"),sQuery(id+"F0.wireOp",EDGE,"E29.trimOffspring"),sQuery(id+"F0.wireOp",EDGE,"E30.trimOffspring")])],"isStart":false});
            var sketch = newSketch(context, id + "F2", { "sketchPlane" : qUnion([Q0])});
            skCircle(sketch, "E31", {"center": v(0, 0) * mm, "radius": 3.18 * mm});
            skSolve(sketch);
        }
        {
            var Q0;
            Q0 = qSketchRegion(id + "F2", true);
            extrude(context, id + "F3", {"entities" : qUnion([Q0]), "operationType" : NewBodyOperationType.REMOVE, "endBound" : BoundingType.THROUGH_ALL, "oppositeDirection" : true, "depth" : 25.4 * mm});
        }
        {
            var Q0;
            Q0=makeQuery(id+"F1.opExtrude","CAP_FACE",FACE,{"disambiguationData":[OSD([sQuery(id+"F0.wireOp",EDGE,"E0"),sQuery(id+"F0.wireOp",EDGE,"E1.trimOffspring"),sQuery(id+"F0.wireOp",EDGE,"E2"),sQuery(id+"F0.wireOp",EDGE,"E3"),sQuery(id+"F0.wireOp",EDGE,"E4.MirrorCS"),sQuery(id+"F0.wireOp",EDGE,"E5.MirrorCS"),sQuery(id+"F0.wireOp",EDGE,"E6.MirrorCS"),sQuery(id+"F0.wireOp",EDGE,"E7.filletArc"),sQuery(id+"F0.wireOp",EDGE,"E8.filletArc"),sQuery(id+"F0.wireOp",EDGE,"E9.filletArc"),sQuery(id+"F0.wireOp",EDGE,"E10.filletArc"),sQuery(id+"F0.wireOp",EDGE,"E11.filletArc"),sQuery(id+"F0.wireOp",EDGE,"E12.filletArc"),sQuery(id+"F0.wireOp",EDGE,"E13.1.0"),sQuery(id+"F0.wireOp",EDGE,"E13.1.1"),sQuery(id+"F0.wireOp",EDGE,"E13.1.2"),sQuery(id+"F0.wireOp",EDGE,"E13.1.3"),sQuery(id+"F0.wireOp",EDGE,"E13.1.4"),sQuery(id+"F0.wireOp",EDGE,"E13.1.5"),sQuery(id+"F0.wireOp",EDGE,"E13.1.6"),sQuery(id+"F0.wireOp",EDGE,"E13.1.7"),sQuery(id+"F0.wireOp",EDGE,"E13.1.8"),sQuery(id+"F0.wireOp",EDGE,"E13.1.9"),sQuery(id+"F0.wireOp",EDGE,"E13.1.10"),sQuery(id+"F0.wireOp",EDGE,"E13.1.11"),sQuery(id+"F0.wireOp",EDGE,"E13.2.0"),sQuery(id+"F0.wireOp",EDGE,"E13.2.1"),sQuery(id+"F0.wireOp",EDGE,"E13.2.2"),sQuery(id+"F0.wireOp",EDGE,"E13.2.3"),sQuery(id+"F0.wireOp",EDGE,"E13.2.4"),sQuery(id+"F0.wireOp",EDGE,"E13.2.5"),sQuery(id+"F0.wireOp",EDGE,"E13.2.6"),sQuery(id+"F0.wireOp",EDGE,"E13.2.7"),sQuery(id+"F0.wireOp",EDGE,"E13.2.8"),sQuery(id+"F0.wireOp",EDGE,"E13.2.9"),sQuery(id+"F0.wireOp",EDGE,"E13.2.10"),sQuery(id+"F0.wireOp",EDGE,"E13.2.11"),sQuery(id+"F0.wireOp",EDGE,"E13.3.0"),sQuery(id+"F0.wireOp",EDGE,"E13.3.1"),sQuery(id+"F0.wireOp",EDGE,"E13.3.2"),sQuery(id+"F0.wireOp",EDGE,"E13.3.3"),sQuery(id+"F0.wireOp",EDGE,"E13.3.4"),sQuery(id+"F0.wireOp",EDGE,"E13.3.5"),sQuery(id+"F0.wireOp",EDGE,"E13.3.6"),sQuery(id+"F0.wireOp",EDGE,"E13.3.7"),sQuery(id+"F0.wireOp",EDGE,"E13.3.8"),sQuery(id+"F0.wireOp",EDGE,"E13.3.9"),sQuery(id+"F0.wireOp",EDGE,"E13.3.10"),sQuery(id+"F0.wireOp",EDGE,"E13.3.11"),sQuery(id+"F0.wireOp",EDGE,"E13.4.0"),sQuery(id+"F0.wireOp",EDGE,"E13.4.1"),sQuery(id+"F0.wireOp",EDGE,"E13.4.2"),sQuery(id+"F0.wireOp",EDGE,"E13.4.3"),sQuery(id+"F0.wireOp",EDGE,"E13.4.4"),sQuery(id+"F0.wireOp",EDGE,"E13.4.5"),sQuery(id+"F0.wireOp",EDGE,"E13.4.6"),sQuery(id+"F0.wireOp",EDGE,"E13.4.7"),sQuery(id+"F0.wireOp",EDGE,"E13.4.8"),sQuery(id+"F0.wireOp",EDGE,"E13.4.9"),sQuery(id+"F0.wireOp",EDGE,"E13.4.10"),sQuery(id+"F0.wireOp",EDGE,"E13.4.11"),sQuery(id+"F0.wireOp",EDGE,"E13.5.0"),sQuery(id+"F0.wireOp",EDGE,"E13.5.1"),sQuery(id+"F0.wireOp",EDGE,"E13.5.2"),sQuery(id+"F0.wireOp",EDGE,"E13.5.3"),sQuery(id+"F0.wireOp",EDGE,"E13.5.4"),sQuery(id+"F0.wireOp",EDGE,"E13.5.5"),sQuery(id+"F0.wireOp",EDGE,"E13.5.6"),sQuery(id+"F0.wireOp",EDGE,"E13.5.7"),sQuery(id+"F0.wireOp",EDGE,"E13.5.8"),sQuery(id+"F0.wireOp",EDGE,"E13.5.9"),sQuery(id+"F0.wireOp",EDGE,"E13.5.10"),sQuery(id+"F0.wireOp",EDGE,"E13.5.11"),sQuery(id+"F0.wireOp",EDGE,"E13.6.0"),sQuery(id+"F0.wireOp",EDGE,"E13.6.1"),sQuery(id+"F0.wireOp",EDGE,"E13.6.2"),sQuery(id+"F0.wireOp",EDGE,"E13.6.3"),sQuery(id+"F0.wireOp",EDGE,"E13.6.4"),sQuery(id+"F0.wireOp",EDGE,"E13.6.5"),sQuery(id+"F0.wireOp",EDGE,"E13.6.6"),sQuery(id+"F0.wireOp",EDGE,"E13.6.7"),sQuery(id+"F0.wireOp",EDGE,"E13.6.8"),sQuery(id+"F0.wireOp",EDGE,"E13.6.9"),sQuery(id+"F0.wireOp",EDGE,"E13.6.10"),sQuery(id+"F0.wireOp",EDGE,"E13.6.11"),sQuery(id+"F0.wireOp",EDGE,"E13.7.0"),sQuery(id+"F0.wireOp",EDGE,"E13.7.1"),sQuery(id+"F0.wireOp",EDGE,"E13.7.2"),sQuery(id+"F0.wireOp",EDGE,"E13.7.3"),sQuery(id+"F0.wireOp",EDGE,"E13.7.4"),sQuery(id+"F0.wireOp",EDGE,"E13.7.5"),sQuery(id+"F0.wireOp",EDGE,"E13.7.6"),sQuery(id+"F0.wireOp",EDGE,"E13.7.7"),sQuery(id+"F0.wireOp",EDGE,"E13.7.8"),sQuery(id+"F0.wireOp",EDGE,"E13.7.9"),sQuery(id+"F0.wireOp",EDGE,"E13.7.10"),sQuery(id+"F0.wireOp",EDGE,"E13.7.11"),sQuery(id+"F0.wireOp",EDGE,"E13.8.0"),sQuery(id+"F0.wireOp",EDGE,"E13.8.1"),sQuery(id+"F0.wireOp",EDGE,"E13.8.2"),sQuery(id+"F0.wireOp",EDGE,"E13.8.3"),sQuery(id+"F0.wireOp",EDGE,"E13.8.4"),sQuery(id+"F0.wireOp",EDGE,"E13.8.5"),sQuery(id+"F0.wireOp",EDGE,"E13.8.6"),sQuery(id+"F0.wireOp",EDGE,"E13.8.7"),sQuery(id+"F0.wireOp",EDGE,"E13.8.8"),sQuery(id+"F0.wireOp",EDGE,"E13.8.9"),sQuery(id+"F0.wireOp",EDGE,"E13.8.10"),sQuery(id+"F0.wireOp",EDGE,"E13.8.11"),sQuery(id+"F0.wireOp",EDGE,"E13.9.0"),sQuery(id+"F0.wireOp",EDGE,"E13.9.1"),sQuery(id+"F0.wireOp",EDGE,"E13.9.2"),sQuery(id+"F0.wireOp",EDGE,"E13.9.3"),sQuery(id+"F0.wireOp",EDGE,"E13.9.4"),sQuery(id+"F0.wireOp",EDGE,"E13.9.5"),sQuery(id+"F0.wireOp",EDGE,"E13.9.6"),sQuery(id+"F0.wireOp",EDGE,"E13.9.7"),sQuery(id+"F0.wireOp",EDGE,"E13.9.8"),sQuery(id+"F0.wireOp",EDGE,"E13.9.9"),sQuery(id+"F0.wireOp",EDGE,"E13.9.10"),sQuery(id+"F0.wireOp",EDGE,"E13.9.11"),sQuery(id+"F0.wireOp",EDGE,"E13.10.0"),sQuery(id+"F0.wireOp",EDGE,"E13.10.1"),sQuery(id+"F0.wireOp",EDGE,"E13.10.2"),sQuery(id+"F0.wireOp",EDGE,"E13.10.3"),sQuery(id+"F0.wireOp",EDGE,"E13.10.4"),sQuery(id+"F0.wireOp",EDGE,"E13.10.5"),sQuery(id+"F0.wireOp",EDGE,"E13.10.6"),sQuery(id+"F0.wireOp",EDGE,"E13.10.7"),sQuery(id+"F0.wireOp",EDGE,"E13.10.8"),sQuery(id+"F0.wireOp",EDGE,"E13.10.9"),sQuery(id+"F0.wireOp",EDGE,"E13.10.10"),sQuery(id+"F0.wireOp",EDGE,"E13.10.11"),sQuery(id+"F0.wireOp",EDGE,"E13.11.0"),sQuery(id+"F0.wireOp",EDGE,"E13.11.1"),sQuery(id+"F0.wireOp",EDGE,"E13.11.2"),sQuery(id+"F0.wireOp",EDGE,"E13.11.3"),sQuery(id+"F0.wireOp",EDGE,"E13.11.4"),sQuery(id+"F0.wireOp",EDGE,"E13.11.5"),sQuery(id+"F0.wireOp",EDGE,"E13.11.6"),sQuery(id+"F0.wireOp",EDGE,"E13.11.7"),sQuery(id+"F0.wireOp",EDGE,"E13.11.8"),sQuery(id+"F0.wireOp",EDGE,"E13.11.9"),sQuery(id+"F0.wireOp",EDGE,"E13.11.10"),sQuery(id+"F0.wireOp",EDGE,"E13.11.11"),sQuery(id+"F0.wireOp",EDGE,"E13.12.0"),sQuery(id+"F0.wireOp",EDGE,"E13.12.1"),sQuery(id+"F0.wireOp",EDGE,"E13.12.2"),sQuery(id+"F0.wireOp",EDGE,"E13.12.3"),sQuery(id+"F0.wireOp",EDGE,"E13.12.4"),sQuery(id+"F0.wireOp",EDGE,"E13.12.5"),sQuery(id+"F0.wireOp",EDGE,"E13.12.6"),sQuery(id+"F0.wireOp",EDGE,"E13.12.7"),sQuery(id+"F0.wireOp",EDGE,"E13.12.8"),sQuery(id+"F0.wireOp",EDGE,"E13.12.9"),sQuery(id+"F0.wireOp",EDGE,"E13.12.10"),sQuery(id+"F0.wireOp",EDGE,"E13.12.11"),sQuery(id+"F0.wireOp",EDGE,"E13.13.0"),sQuery(id+"F0.wireOp",EDGE,"E13.13.1"),sQuery(id+"F0.wireOp",EDGE,"E13.13.2"),sQuery(id+"F0.wireOp",EDGE,"E13.13.3"),sQuery(id+"F0.wireOp",EDGE,"E13.13.4"),sQuery(id+"F0.wireOp",EDGE,"E13.13.5"),sQuery(id+"F0.wireOp",EDGE,"E13.13.6"),sQuery(id+"F0.wireOp",EDGE,"E13.13.7"),sQuery(id+"F0.wireOp",EDGE,"E13.13.8"),sQuery(id+"F0.wireOp",EDGE,"E13.13.9"),sQuery(id+"F0.wireOp",EDGE,"E13.13.10"),sQuery(id+"F0.wireOp",EDGE,"E13.13.11"),sQuery(id+"F0.wireOp",EDGE,"E13.14.0"),sQuery(id+"F0.wireOp",EDGE,"E13.14.1"),sQuery(id+"F0.wireOp",EDGE,"E13.14.2"),sQuery(id+"F0.wireOp",EDGE,"E13.14.3"),sQuery(id+"F0.wireOp",EDGE,"E13.14.4"),sQuery(id+"F0.wireOp",EDGE,"E13.14.5"),sQuery(id+"F0.wireOp",EDGE,"E13.14.6"),sQuery(id+"F0.wireOp",EDGE,"E13.14.7"),sQuery(id+"F0.wireOp",EDGE,"E13.14.8"),sQuery(id+"F0.wireOp",EDGE,"E13.14.9"),sQuery(id+"F0.wireOp",EDGE,"E13.14.10"),sQuery(id+"F0.wireOp",EDGE,"E13.14.11"),sQuery(id+"F0.wireOp",EDGE,"E13.15.0"),sQuery(id+"F0.wireOp",EDGE,"E13.15.1"),sQuery(id+"F0.wireOp",EDGE,"E13.15.2"),sQuery(id+"F0.wireOp",EDGE,"E13.15.3"),sQuery(id+"F0.wireOp",EDGE,"E13.15.4"),sQuery(id+"F0.wireOp",EDGE,"E13.15.5"),sQuery(id+"F0.wireOp",EDGE,"E13.15.6"),sQuery(id+"F0.wireOp",EDGE,"E13.15.7"),sQuery(id+"F0.wireOp",EDGE,"E13.15.8"),sQuery(id+"F0.wireOp",EDGE,"E13.15.9"),sQuery(id+"F0.wireOp",EDGE,"E13.15.10"),sQuery(id+"F0.wireOp",EDGE,"E13.15.11"),sQuery(id+"F0.wireOp",EDGE,"E13.16.0"),sQuery(id+"F0.wireOp",EDGE,"E13.16.1"),sQuery(id+"F0.wireOp",EDGE,"E13.16.2"),sQuery(id+"F0.wireOp",EDGE,"E13.16.3"),sQuery(id+"F0.wireOp",EDGE,"E13.16.4"),sQuery(id+"F0.wireOp",EDGE,"E13.16.5"),sQuery(id+"F0.wireOp",EDGE,"E13.16.6"),sQuery(id+"F0.wireOp",EDGE,"E13.16.7"),sQuery(id+"F0.wireOp",EDGE,"E13.16.8"),sQuery(id+"F0.wireOp",EDGE,"E13.16.9"),sQuery(id+"F0.wireOp",EDGE,"E13.16.10"),sQuery(id+"F0.wireOp",EDGE,"E13.16.11"),sQuery(id+"F0.wireOp",EDGE,"E13.17.0"),sQuery(id+"F0.wireOp",EDGE,"E13.17.1"),sQuery(id+"F0.wireOp",EDGE,"E13.17.2"),sQuery(id+"F0.wireOp",EDGE,"E13.17.3"),sQuery(id+"F0.wireOp",EDGE,"E13.17.4"),sQuery(id+"F0.wireOp",EDGE,"E13.17.5"),sQuery(id+"F0.wireOp",EDGE,"E13.17.6"),sQuery(id+"F0.wireOp",EDGE,"E13.17.7"),sQuery(id+"F0.wireOp",EDGE,"E13.17.8"),sQuery(id+"F0.wireOp",EDGE,"E13.17.9"),sQuery(id+"F0.wireOp",EDGE,"E13.17.10"),sQuery(id+"F0.wireOp",EDGE,"E13.17.11"),sQuery(id+"F0.wireOp",EDGE,"E14.trimOffspring"),sQuery(id+"F0.wireOp",EDGE,"E15.trimOffspring"),sQuery(id+"F0.wireOp",EDGE,"E16.trimOffspring"),sQuery(id+"F0.wireOp",EDGE,"E17.trimOffspring"),sQuery(id+"F0.wireOp",EDGE,"E18.trimOffspring"),sQuery(id+"F0.wireOp",EDGE,"E19.trimOffspring"),sQuery(id+"F0.wireOp",EDGE,"E20.trimOffspring"),sQuery(id+"F0.wireOp",EDGE,"E21.trimOffspring"),sQuery(id+"F0.wireOp",EDGE,"E22.trimOffspring"),sQuery(id+"F0.wireOp",EDGE,"E23.trimOffspring"),sQuery(id+"F0.wireOp",EDGE,"E24.trimOffspring"),sQuery(id+"F0.wireOp",EDGE,"E25.trimOffspring"),sQuery(id+"F0.wireOp",EDGE,"E26.trimOffspring"),sQuery(id+"F0.wireOp",EDGE,"E27.trimOffspring"),sQuery(id+"F0.wireOp",EDGE,"E28.trimOffspring"),sQuery(id+"F0.wireOp",EDGE,"E29.trimOffspring"),sQuery(id+"F0.wireOp",EDGE,"E30.trimOffspring")])],"isStart":false});
            shell(context, id + "F4", {"entities" : qUnion([Q0]), "thickness" : 5.08 * mm});
        }
        {
            var Q0;
            Q0=qCreatedBy(makeId("Right.planeOp"),FACE);
            cPlane(context, id + "F5", {"entities" : qUnion([Q0]), "cplaneType" : CPlaneType.OFFSET, "offset" : 8.25 * mm, "width" : 152.4 * mm, "height" : 152.4 * mm});
        }
        {
            var Q0;
            Q0=qCreatedBy(id+"F5.planeOp",FACE);
            var sketch = newSketch(context, id + "F6", { "sketchPlane" : qUnion([Q0])});
            skCircle(sketch, "E32", {"center": v(-9.53, 0) * mm, "radius": 1.13 * mm});
            skSolve(sketch);
        }
        {
            var Q0;
            Q0 = qSketchRegion(id + "F6", true);
            extrude(context, id + "F7", {"entities" : qUnion([Q0]), "operationType" : NewBodyOperationType.REMOVE, "oppositeDirection" : true, "depth" : 8.25 * mm});
        }
    });
